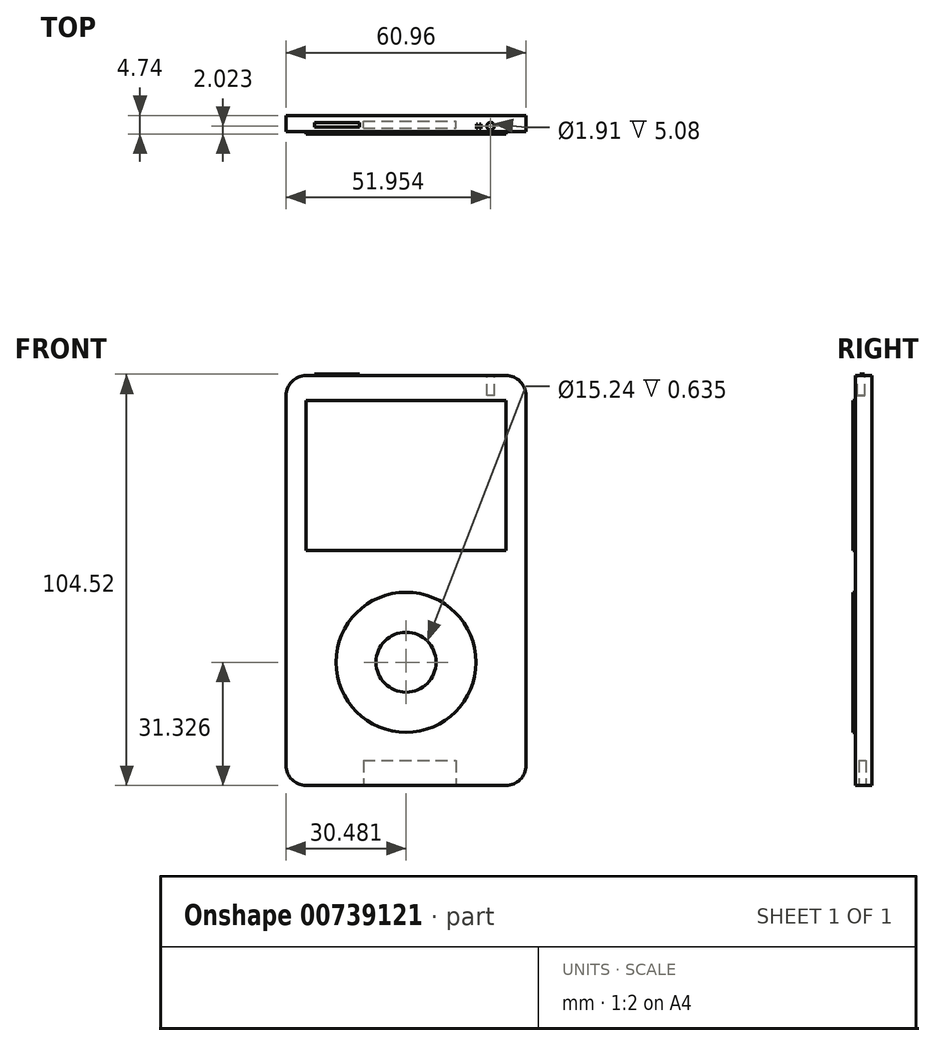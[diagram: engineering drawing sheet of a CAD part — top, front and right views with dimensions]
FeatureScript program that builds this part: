
annotation { "Feature Type Name" : "Feature", "Feature Type Description" : "" }
export const myFeature = defineFeature(function(context is Context, id is Id, definition is map)
    precondition{}
    {
        {
            var Q0;
            Q0=qCreatedBy(makeId("Front.planeOp"),FACE);
            var sketch = newSketch(context, id + "F0", { "sketchPlane" : qUnion([Q0])});
            skLineSegment(sketch, "E0.bottom", {"start": v(-26.87, 44.58) * mm, "end": v(34.1, 44.58) * mm});
            skLineSegment(sketch, "E0.top", {"start": v(-26.87, -59.56) * mm, "end": v(34.1, -59.56) * mm});
            skLineSegment(sketch, "E0.left", {"start": v(-26.87, 44.58) * mm, "end": v(-26.87, -59.56) * mm});
            skLineSegment(sketch, "E0.right", {"start": v(34.1, 44.58) * mm, "end": v(34.1, -59.56) * mm});
            skSolve(sketch);
        }
        {
            var Q0;
            Q0 = qSketchRegion(id + "F0", true);
            extrude(context, id + "F1", {"entities" : qUnion([Q0]), "depth" : 4.1 * mm, "offsetDistance" : 25.4 * mm});
        }
        {
            var Q0;
            Q0=makeQuery(id+"F1.opExtrude","CAP_FACE",FACE,{"disambiguationData":[OSD([sQuery(id+"F0.wireOp",EDGE,"E0.bottom"),sQuery(id+"F0.wireOp",EDGE,"E0.top"),sQuery(id+"F0.wireOp",EDGE,"E0.left"),sQuery(id+"F0.wireOp",EDGE,"E0.right")])],"isStart":false});
            var sketch = newSketch(context, id + "F2", { "sketchPlane" : qUnion([Q0])});
            skLineSegment(sketch, "E1.bottom", {"start": v(-21.79, 38.23) * mm, "end": v(29.01, 38.23) * mm});
            skLineSegment(sketch, "E1.top", {"start": v(-21.79, 0.13) * mm, "end": v(29.01, 0.13) * mm});
            skLineSegment(sketch, "E1.left", {"start": v(-21.79, 38.23) * mm, "end": v(-21.79, 0.13) * mm});
            skLineSegment(sketch, "E1.right", {"start": v(29.01, 38.23) * mm, "end": v(29.01, 0.13) * mm});
            skPoint(sketch, "E2", {"position": v(29.01, 19.18) * mm});
            skCircle(sketch, "E3", {"center": v(3.61, -28.23) * mm, "radius": 17.78 * mm});
            skLineSegment(sketch, "E4.trimOffspring", {"start": v(3.61, 38.23) * mm, "end": v(3.61, 44.58) * mm, "construction": true});
            skPoint(sketch, "E5.start.orphan", {"position": v(3.61, -59.56) * mm});
            skCircle(sketch, "E6", {"center": v(3.61, -28.23) * mm, "radius": 7.62 * mm});
            skSolve(sketch);
        }
        {
            var Q0;
            Q0 = qSketchRegion(id + "F2", true);
            extrude(context, id + "F3", {"entities" : qUnion([Q0]), "operationType" : NewBodyOperationType.ADD, "depth" : 0.64 * mm, "offsetDistance" : 25.4 * mm});
        }
        {
            var Q0;
            Q0=makeQuery(id+"F1.opExtrude","SWEPT_EDGE",EDGE,{"disambiguationData":[OSD([sQuery(id+"F0.wireOp",EDGE,"E0.bottom"),sQuery(id+"F0.wireOp",EDGE,"E0.left")])]});
            var Q1;
            Q1=makeQuery(id+"F1.opExtrude","SWEPT_EDGE",EDGE,{"disambiguationData":[OSD([sQuery(id+"F0.wireOp",EDGE,"E0.bottom"),sQuery(id+"F0.wireOp",EDGE,"E0.right")])]});
            var Q2;
            Q2=makeQuery(id+"F1.opExtrude","SWEPT_EDGE",EDGE,{"disambiguationData":[OSD([sQuery(id+"F0.wireOp",EDGE,"E0.top"),sQuery(id+"F0.wireOp",EDGE,"E0.right")])]});
            var Q3;
            Q3=makeQuery(id+"F1.opExtrude","SWEPT_EDGE",EDGE,{"disambiguationData":[OSD([sQuery(id+"F0.wireOp",EDGE,"E0.top"),sQuery(id+"F0.wireOp",EDGE,"E0.left")])]});
            fillet(context, id + "F4", {"entities" : qUnion([Q0, Q1, Q2, Q3]), "radius" : 5.08 * mm, "tangentPropagation" : true, "allowEdgeOverflow" : false});
        }
        {
            var Q0;
            Q0=makeQuery(id+"F1.opExtrude","SWEPT_FACE",FACE,{"disambiguationData":[OSD([sQuery(id+"F0.wireOp",EDGE,"E0.bottom")])]});
            var sketch = newSketch(context, id + "F5", { "sketchPlane" : qUnion([Q0])});
            skCircle(sketch, "E7", {"center": v(25.84, -8.36) * mm, "radius": 1.27 * mm});
            skSolve(sketch);
        }
        {
            var Q0;
            Q0 = qSketchRegion(id + "F5", true);
            extrude(context, id + "F6", {"entities" : qUnion([Q0]), "operationType" : NewBodyOperationType.REMOVE, "oppositeDirection" : true, "depth" : 3.8 * mm, "offsetDistance" : 25.4 * mm});
        }
        {
            var Q0;
            Q0=makeQuery(id+"F1.opExtrude","SWEPT_FACE",FACE,{"disambiguationData":[OSD([sQuery(id+"F0.wireOp",EDGE,"E0.bottom")])]});
            var sketch = newSketch(context, id + "F7", { "sketchPlane" : qUnion([Q0])});
            skLineSegment(sketch, "E8.bottom", {"start": v(23.34, -8.18) * mm, "end": v(23.47, -8.18) * mm});
            skLineSegment(sketch, "E8.top", {"start": v(23.34, -8.82) * mm, "end": v(23.47, -8.82) * mm});
            skLineSegment(sketch, "E8.left", {"start": v(23.34, -8.18) * mm, "end": v(23.34, -8.82) * mm});
            skLineSegment(sketch, "E8.right", {"start": v(23.47, -8.18) * mm, "end": v(23.47, -8.82) * mm});
            skLineSegment(sketch, "E9.bottom", {"start": v(23.7, -8.18) * mm, "end": v(23.82, -8.18) * mm});
            skLineSegment(sketch, "E9.top", {"start": v(23.7, -8.83) * mm, "end": v(23.82, -8.83) * mm});
            skLineSegment(sketch, "E9.left", {"start": v(23.7, -8.18) * mm, "end": v(23.7, -8.83) * mm});
            skLineSegment(sketch, "E9.right", {"start": v(23.82, -8.18) * mm, "end": v(23.82, -8.83) * mm});
            skSolve(sketch);
        }
        {
            var Q0;
            Q0 = qSketchRegion(id + "F7", true);
            extrude(context, id + "F8", {"entities" : qUnion([Q0]), "operationType" : NewBodyOperationType.REMOVE, "oppositeDirection" : true, "depth" : 0.06 * mm, "offsetDistance" : 25.4 * mm});
        }
        {
            var Q0;
            Q0=makeQuery(id+"F1.opExtrude","SWEPT_FACE",FACE,{"disambiguationData":[OSD([sQuery(id+"F0.wireOp",EDGE,"E0.top")])]});
            var sketch = newSketch(context, id + "F9", { "sketchPlane" : qUnion([Q0])});
            skLineSegment(sketch, "E10.bottom", {"start": v(-7.26, 3.21) * mm, "end": v(16.31, 3.21) * mm});
            skLineSegment(sketch, "E10.top", {"start": v(-7.26, 1.42) * mm, "end": v(16.31, 1.42) * mm});
            skLineSegment(sketch, "E10.left", {"start": v(-7.26, 3.21) * mm, "end": v(-7.26, 1.42) * mm});
            skLineSegment(sketch, "E10.right", {"start": v(16.31, 3.21) * mm, "end": v(16.31, 1.42) * mm});
            skSolve(sketch);
        }
        {
            var Q0;
            Q0 = qSketchRegion(id + "F9", true);
            extrude(context, id + "F10", {"entities" : qUnion([Q0]), "operationType" : NewBodyOperationType.REMOVE, "oppositeDirection" : true, "depth" : 6.35 * mm, "offsetDistance" : 25.4 * mm});
        }
        {
            var Q0;
            Q0=makeQuery(id+"F1.opExtrude","SWEPT_FACE",FACE,{"disambiguationData":[OSD([sQuery(id+"F0.wireOp",EDGE,"E0.bottom")])]});
            var sketch = newSketch(context, id + "F11", { "sketchPlane" : qUnion([Q0])});
            skLineSegment(sketch, "E11.bottom", {"start": v(-19.6, -1.87) * mm, "end": v(-8.17, -1.87) * mm});
            skLineSegment(sketch, "E11.top", {"start": v(-19.6, -3.02) * mm, "end": v(-8.17, -3.02) * mm});
            skLineSegment(sketch, "E11.left", {"start": v(-19.6, -1.87) * mm, "end": v(-19.6, -3.02) * mm});
            skLineSegment(sketch, "E11.right", {"start": v(-8.17, -1.87) * mm, "end": v(-8.17, -3.02) * mm});
            skSolve(sketch);
        }
        {
            var Q0;
            Q0 = qSketchRegion(id + "F11", true);
            extrude(context, id + "F12", {"entities" : qUnion([Q0]), "operationType" : NewBodyOperationType.ADD, "depth" : 0.38 * mm, "offsetDistance" : 25.4 * mm});
        }
        {
            var Q0;
            Q0=makeQuery(id+"F1.opExtrude","SWEPT_FACE",FACE,{"disambiguationData":[OSD([sQuery(id+"F0.wireOp",EDGE,"E0.bottom")])]});
            var sketch = newSketch(context, id + "F13", { "sketchPlane" : qUnion([Q0])});
            skCircle(sketch, "E12", {"center": v(25.08, -2.72) * mm, "radius": 0.95 * mm});
            skSolve(sketch);
        }
        {
            var Q0;
            Q0 = qSketchRegion(id + "F13", true);
            extrude(context, id + "F14", {"entities" : qUnion([Q0]), "operationType" : NewBodyOperationType.REMOVE, "oppositeDirection" : true, "depth" : 5.08 * mm, "offsetDistance" : 25.4 * mm});
        }
        {
            var Q0;
            Q0=makeQuery(id+"F1.opExtrude","SWEPT_FACE",FACE,{"disambiguationData":[OSD([sQuery(id+"F0.wireOp",EDGE,"E0.bottom")])]});
            var sketch = newSketch(context, id + "F15", { "sketchPlane" : qUnion([Q0])});
            skLineSegment(sketch, "E13.bottom", {"start": v(21.78, -2.18) * mm, "end": v(21.46, -2.18) * mm});
            skLineSegment(sketch, "E13.top", {"start": v(21.78, -3.3) * mm, "end": v(21.46, -3.3) * mm});
            skLineSegment(sketch, "E13.left", {"start": v(21.78, -2.18) * mm, "end": v(21.78, -3.3) * mm});
            skLineSegment(sketch, "E13.right", {"start": v(21.46, -2.18) * mm, "end": v(21.46, -3.3) * mm});
            skLineSegment(sketch, "E14.bottom", {"start": v(22.32, -2.18) * mm, "end": v(22.64, -2.18) * mm});
            skLineSegment(sketch, "E14.top", {"start": v(22.32, -3.3) * mm, "end": v(22.64, -3.3) * mm});
            skLineSegment(sketch, "E14.left", {"start": v(22.32, -2.18) * mm, "end": v(22.32, -3.3) * mm});
            skLineSegment(sketch, "E14.right", {"start": v(22.64, -2.18) * mm, "end": v(22.64, -3.3) * mm});
            skSolve(sketch);
        }
        {
            var Q0;
            Q0 = qSketchRegion(id + "F15", true);
            extrude(context, id + "F16", {"entities" : qUnion([Q0]), "operationType" : NewBodyOperationType.ADD, "depth" : 0.04 * mm, "offsetDistance" : 25.4 * mm});
        }
    });
